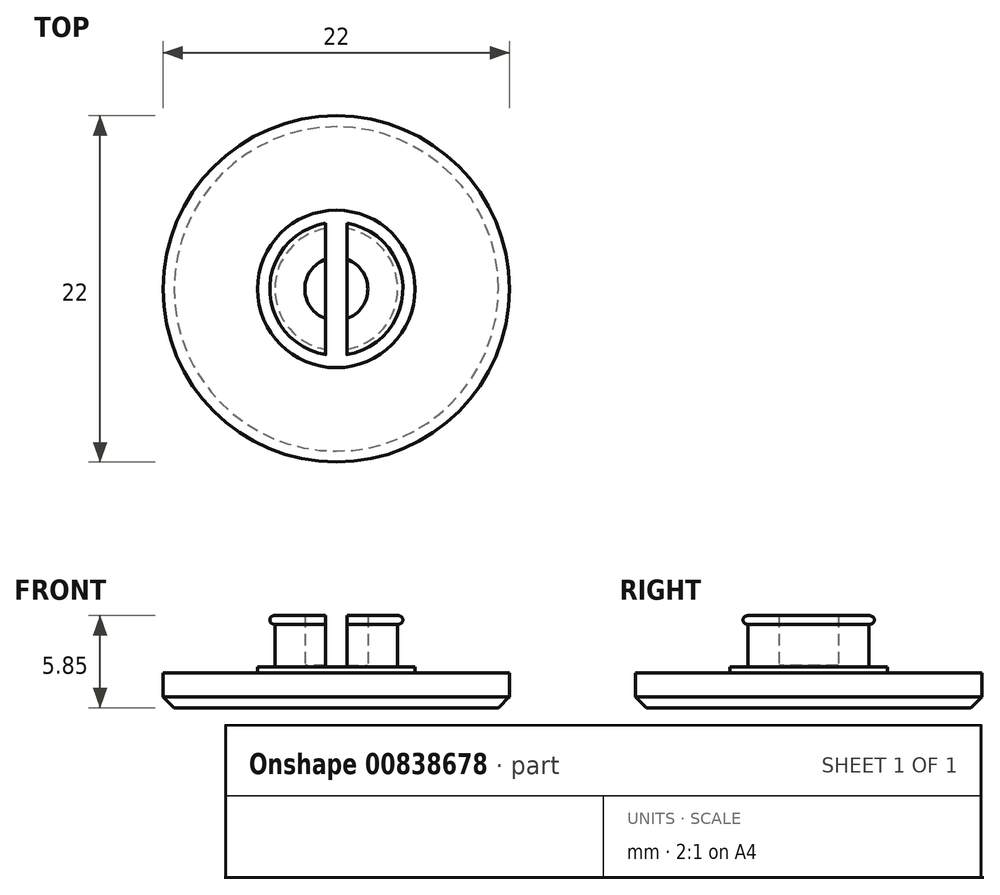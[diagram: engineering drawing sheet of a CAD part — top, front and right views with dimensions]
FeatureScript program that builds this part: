
annotation { "Feature Type Name" : "Feature", "Feature Type Description" : "" }
export const myFeature = defineFeature(function(context is Context, id is Id, definition is map)
    precondition{}
    {
        {
            var Q0;
            Q0=qCreatedBy(makeId("Top.planeOp"),FACE);
            var sketch = newSketch(context, id + "F0", { "sketchPlane" : qUnion([Q0])});
            skCircle(sketch, "E0", {"center": v(0, 0) * mm, "radius": 11 * mm});
            skSolve(sketch);
        }
        {
            var Q0;
            Q0=makeQuery(id+"F0.imprint","IMPRINT",FACE,{"disambiguationData":[TD([[makeQuery(id+"F0.imprint","IMPRINT",EDGE,{"derivedFrom":sQuery(id+"F0.wireOp",EDGE,"E0")}),1.0]])]});
            extrude(context, id + "F1", {"entities" : qUnion([Q0]), "depth" : 2.2 * mm, "offsetDistance" : 25 * mm});
        }
        {
            var Q0;
            Q0=makeQuery(id+"F1.opExtrude","CAP_EDGE",EDGE,{"disambiguationData":[OSD([sQuery(id+"F0.wireOp",EDGE,"E0")])],"isStart":true});
            chamfer(context, id + "F2", {"entities" : qUnion([Q0]), "chamferType" : ChamferType.OFFSET_ANGLE, "width" : 0.7 * mm, "oppositeDirection" : false, "angle" : 45 * degree, "tangentPropagation" : true});
        }
        {
            var Q0;
            Q0=qCreatedBy(makeId("Top.planeOp"),FACE);
            var sketch = newSketch(context, id + "F3", { "sketchPlane" : qUnion([Q0])});
            skCircle(sketch, "E1", {"center": v(0, 0) * mm, "radius": 5 * mm});
            skSolve(sketch);
        }
        {
            var Q0;
            Q0=qSketchRegion(id+"F3",true);
            extrude(context, id + "F4", {"entities" : qUnion([Q0]), "operationType" : NewBodyOperationType.ADD, "depth" : 2.6 * mm, "offsetDistance" : 25 * mm});
        }
        {
            var Q0;
            Q0=qCreatedBy(makeId("Top.planeOp"),FACE);
            var sketch = newSketch(context, id + "F5", { "sketchPlane" : qUnion([Q0])});
            skCircle(sketch, "E2", {"center": v(0, 0) * mm, "radius": 3.9 * mm});
            skSolve(sketch);
        }
        {
            var Q0;
            Q0=qSketchRegion(id+"F5",true);
            extrude(context, id + "F6", {"entities" : qUnion([Q0]), "operationType" : NewBodyOperationType.ADD, "depth" : 5.85 * mm, "offsetDistance" : 25 * mm});
        }
        {
            var Q0;
            Q0=qCreatedBy(makeId("Top.planeOp"),FACE);
            var sketch = newSketch(context, id + "F7", { "sketchPlane" : qUnion([Q0])});
            skCircle(sketch, "E3", {"center": v(0, 0) * mm, "radius": 4.22 * mm});
            skSolve(sketch);
        }
        {
            var Q0;
            Q0=makeQuery(id+"F7.imprint","IMPRINT",FACE,{"disambiguationData":[TD([[makeQuery(id+"F7.imprint","IMPRINT",EDGE,{"derivedFrom":sQuery(id+"F7.wireOp",EDGE,"E3")}),1.0]])]});
            extrude(context, id + "F8", {"entities" : qUnion([Q0]), "operationType" : NewBodyOperationType.ADD, "depth" : 5.85 * mm, "offsetDistance" : 25 * mm, "hasSecondDirection" : true, "secondDirectionOppositeDirection" : false, "secondDirectionDepth" : 5.3 * mm});
        }
        {
            var Q0;
            Q0=makeQuery(id+"F8.opExtrude","SWEPT_FACE",FACE,{"disambiguationData":[OSD([sQuery(id+"F7.wireOp",EDGE,"E3")])]});
            fillet(context, id + "F9", {"entities" : qUnion([Q0]), "radius" : 0.28 * mm, "tangentPropagation" : true, "allowEdgeOverflow" : false});
        }
        {
            var Q0;
            Q0=qCreatedBy(makeId("Front.planeOp"),FACE);
            var sketch = newSketch(context, id + "F10", { "sketchPlane" : qUnion([Q0])});
            skLineSegment(sketch, "E4.bottom", {"start": v(0.67, 6.6) * mm, "end": v(-0.67, 6.6) * mm});
            skLineSegment(sketch, "E4.top", {"start": v(0.67, 2.6) * mm, "end": v(-0.67, 2.6) * mm});
            skLineSegment(sketch, "E4.left", {"start": v(0.67, 6.6) * mm, "end": v(0.67, 2.6) * mm});
            skLineSegment(sketch, "E4.right", {"start": v(-0.67, 6.6) * mm, "end": v(-0.67, 2.6) * mm});
            skPoint(sketch, "E4.middle", {"position": v(0, 4.6) * mm});
            skSolve(sketch);
        }
        {
            var Q0;
            Q0=makeQuery(id+"F10.imprint","IMPRINT",FACE,{"disambiguationData":[TD([[makeQuery(id+"F10.imprint","IMPRINT",EDGE,{"derivedFrom":sQuery(id+"F10.wireOp",EDGE,"E4.bottom")}),1.0]])]});
            extrude(context, id + "F11", {"entities" : qUnion([Q0]), "operationType" : NewBodyOperationType.REMOVE, "endBound" : BoundingType.SYMMETRIC, "oppositeDirection" : true, "depth" : 25 * mm, "offsetDistance" : 25 * mm});
        }
        {
            var Q0;
            Q0=qCreatedBy(makeId("Top.planeOp"),FACE);
            var sketch = newSketch(context, id + "F12", { "sketchPlane" : qUnion([Q0])});
            skCircle(sketch, "E5", {"center": v(0, 0) * mm, "radius": 2 * mm});
            skSolve(sketch);
        }
        {
            var Q0;
            Q0=makeQuery(id+"F12.imprint","IMPRINT",FACE,{"disambiguationData":[TD([[makeQuery(id+"F12.imprint","IMPRINT",EDGE,{"derivedFrom":sQuery(id+"F12.wireOp",EDGE,"E5")}),1.0]])]});
            extrude(context, id + "F13", {"entities" : qUnion([Q0]), "operationType" : NewBodyOperationType.REMOVE, "depth" : 7 * mm, "offsetDistance" : 25 * mm, "hasSecondDirection" : true, "secondDirectionOppositeDirection" : false, "secondDirectionDepth" : 2.69 * mm});
        }
    });
